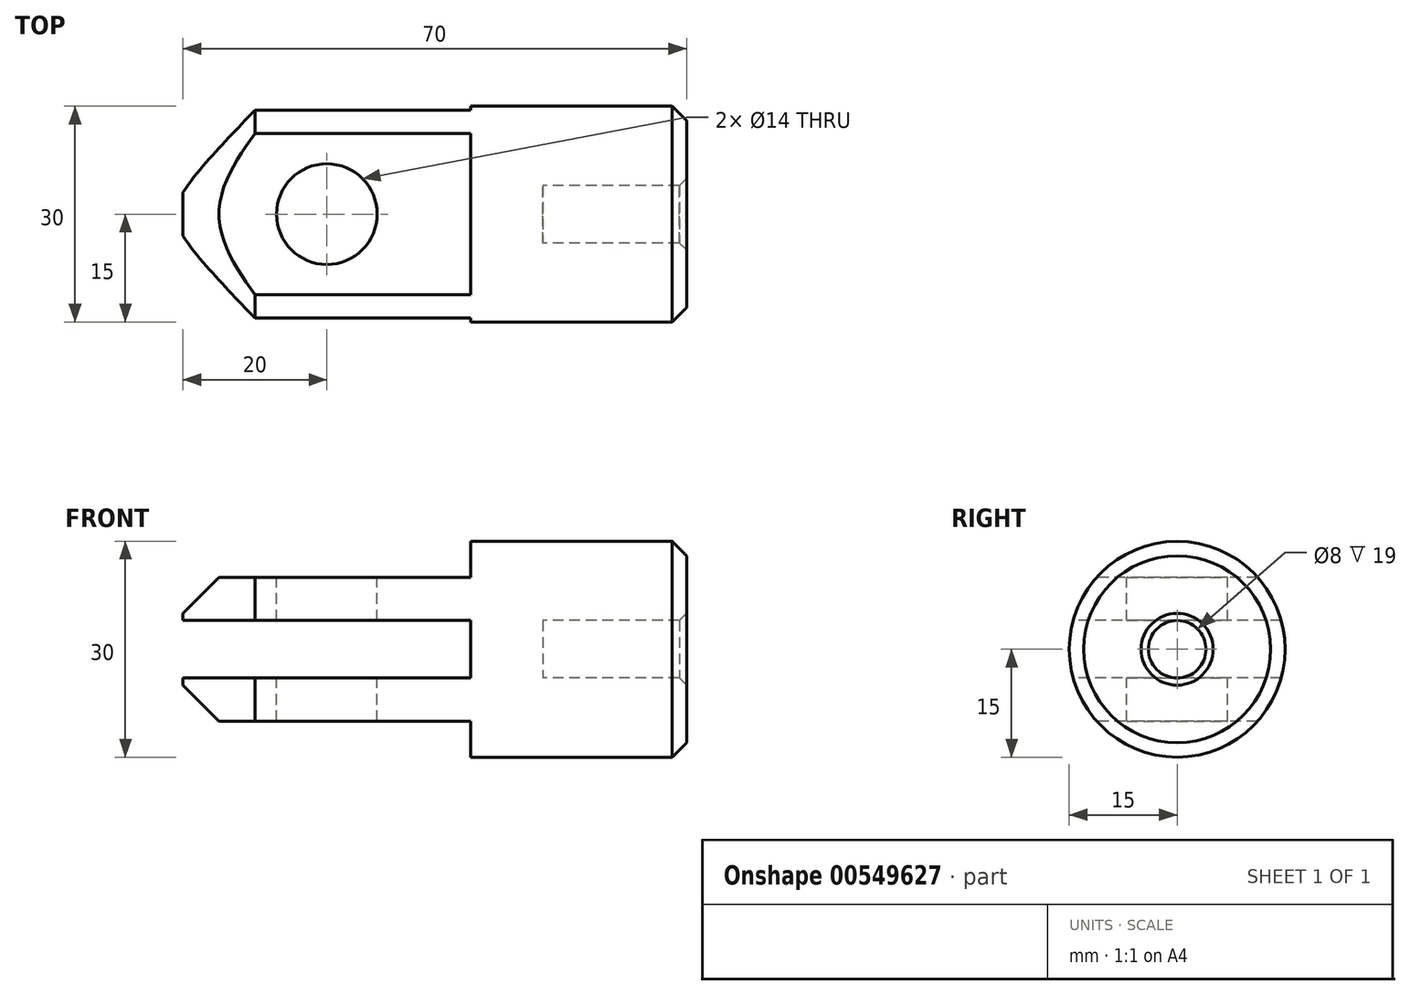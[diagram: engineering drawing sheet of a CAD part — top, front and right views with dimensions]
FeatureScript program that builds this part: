
annotation { "Feature Type Name" : "Feature", "Feature Type Description" : "" }
export const myFeature = defineFeature(function(context is Context, id is Id, definition is map)
    precondition{}
    {
        {
            var Q0;
            Q0=qCreatedBy(makeId("Front.planeOp"),FACE);
            var sketch = newSketch(context, id + "F0", { "sketchPlane" : qUnion([Q0])});
            skLineSegment(sketch, "E0", {"start": v(0, 0) * mm, "end": v(0, 4) * mm});
            skLineSegment(sketch, "E1", {"start": v(0, 4) * mm, "end": v(20, 4) * mm});
            skLineSegment(sketch, "E2", {"start": v(20, 4) * mm, "end": v(20, 15) * mm});
            skLineSegment(sketch, "E3", {"start": v(20, 15) * mm, "end": v(-50, 15) * mm});
            skLineSegment(sketch, "E4", {"start": v(-50, 15) * mm, "end": v(-50, 0) * mm});
            skLineSegment(sketch, "E5", {"start": v(-50, 0) * mm, "end": v(0, 0) * mm});
            skSolve(sketch);
        }
        {
            var Q0;
            Q0=makeQuery(id+"F0.imprint","IMPRINT",FACE,{"disambiguationData":[TD([[makeQuery(id+"F0.imprint","IMPRINT",EDGE,{"derivedFrom":sQuery(id+"F0.wireOp",EDGE,"E0")}),1.0]])]});
            var Q1;
            Q1=sQuery(id+"F0.wireOp",EDGE,"E5");
            revolve(context, id + "F1", {"entities" : qUnion([Q0]), "axis" : qUnion([Q1]), "revolveType" : RevolveType.FULL});
        }
        {
            var Q0;
            Q0=qCreatedBy(makeId("Front.planeOp"),FACE);
            var sketch = newSketch(context, id + "F2", { "sketchPlane" : qUnion([Q0])});
            skLineSegment(sketch, "E6", {"start": v(-60.62, 0) * mm, "end": v(-60.62, 4) * mm});
            skLineSegment(sketch, "E7", {"start": v(-55.02, 4) * mm, "end": v(-10, 4) * mm});
            skLineSegment(sketch, "E8", {"start": v(-60.62, 15) * mm, "end": v(-10, 15) * mm});
            skLineSegment(sketch, "E9.0", {"start": v(-55.02, 10) * mm, "end": v(-10, 10) * mm});
            skPoint(sketch, "E10.endSnap0", {"position": v(0, 15) * mm});
            skLineSegment(sketch, "E11.0", {"start": v(-10, -2) * mm, "end": v(-10, 4) * mm});
            skLineSegment(sketch, "E12", {"start": v(-60.62, 4) * mm, "end": v(-60.62, 15) * mm});
            skPoint(sketch, "E13.orphan", {"position": v(-50, 15) * mm});
            skPoint(sketch, "E14.orphan", {"position": v(0, 19.13) * mm});
            skPoint(sketch, "E15.orphan", {"position": v(50, 15) * mm});
            skLineSegment(sketch, "E16.trimOffspring", {"start": v(-10, 10) * mm, "end": v(-10, 15) * mm});
            skPoint(sketch, "E17.orphan", {"position": v(0, 4) * mm});
            skLineSegment(sketch, "E18", {"start": v(-55.02, 10) * mm, "end": v(-55.02, 4) * mm});
            skPoint(sketch, "E19.orphan", {"position": v(-60.62, 10) * mm});
            skLineSegment(sketch, "E20.MirrorCS", {"start": v(-10, -10) * mm, "end": v(-10, -15) * mm});
            skLineSegment(sketch, "E21.MirrorCS", {"start": v(-55.02, -10) * mm, "end": v(-55.02, -4) * mm});
            skLineSegment(sketch, "E22.MirrorCS", {"start": v(-60.62, -4) * mm, "end": v(-60.62, -15) * mm});
            skLineSegment(sketch, "E23.MirrorCS", {"start": v(-60.62, -15) * mm, "end": v(-10, -15) * mm});
            skLineSegment(sketch, "E24.MirrorCS", {"start": v(-55.02, -4) * mm, "end": v(-10, -4) * mm});
            skLineSegment(sketch, "E25.MirrorCS", {"start": v(-60.62, 0) * mm, "end": v(-60.62, -4) * mm});
            skPoint(sketch, "E26.MirrorP", {"position": v(-60.62, -10) * mm});
            skPoint(sketch, "E27.MirrorP", {"position": v(-50, -15) * mm});
            skLineSegment(sketch, "E28.MirrorCS", {"start": v(-10, 2) * mm, "end": v(-10, -4) * mm});
            skLineSegment(sketch, "E29.MirrorCS", {"start": v(-55.02, -10) * mm, "end": v(-10, -10) * mm});
            skSolve(sketch);
        }
        {
            var Q0;
            Q0=makeQuery(id+"F1.opRevolve","SWEPT_EDGE",EDGE,{"disambiguationData":[OSD([sQuery(id+"F0.wireOp",EDGE,"E3"),sQuery(id+"F0.wireOp",EDGE,"E4")])]});
            chamfer(context, id + "F3", {"entities" : qUnion([Q0]), "width" : 10 * mm, "tangentPropagation" : true});
        }
        {
            var Q0;
            Q0=makeQuery(id+"F2.imprint","IMPRINT",FACE,{"disambiguationData":[TD([[makeQuery(id+"F2.imprint","IMPRINT",EDGE,{"derivedFrom":sQuery(id+"F2.wireOp",EDGE,"E6")}),-1.0]])]});
            extrude(context, id + "F4", {"entities" : qUnion([Q0]), "operationType" : NewBodyOperationType.REMOVE, "endBound" : BoundingType.SYMMETRIC, "oppositeDirection" : true, "depth" : 50 * mm, "offsetDistance" : 25 * mm});
        }
        {
            var Q0;
            Q0=qCreatedBy(makeId("Top.planeOp"),FACE);
            var sketch = newSketch(context, id + "F5", { "sketchPlane" : qUnion([Q0])});
            skCircle(sketch, "E30", {"center": v(-30, 0) * mm, "radius": 7 * mm});
            skSolve(sketch);
        }
        {
            var Q0;
            Q0=makeQuery(id+"F5.imprint","IMPRINT",FACE,{"disambiguationData":[TD([[makeQuery(id+"F5.imprint","IMPRINT",EDGE,{"derivedFrom":sQuery(id+"F5.wireOp",EDGE,"E30")}),1.0]])]});
            var Q1;
            Q1=sQuery(id+"F5.wireOp",EDGE,"E30");
            extrude(context, id + "F6", {"entities" : qUnion([Q0]), "operationType" : NewBodyOperationType.REMOVE, "surfaceEntities" : qUnion([Q1]), "endBound" : BoundingType.SYMMETRIC, "oppositeDirection" : true, "depth" : 50 * mm, "offsetDistance" : 25 * mm});
        }
        {
            var Q0;
            Q0=makeQuery(id+"F1.opRevolve","SWEPT_EDGE",EDGE,{"disambiguationData":[OSD([sQuery(id+"F0.wireOp",EDGE,"E2"),sQuery(id+"F0.wireOp",EDGE,"E3")])]});
            chamfer(context, id + "F7", {"entities" : qUnion([Q0]), "width" : 2 * mm, "tangentPropagation" : true});
        }
        {
            var Q0;
            Q0=makeQuery(id+"F1.opRevolve","SWEPT_EDGE",EDGE,{"disambiguationData":[OSD([sQuery(id+"F0.wireOp",EDGE,"E1"),sQuery(id+"F0.wireOp",EDGE,"E2")])]});
            chamfer(context, id + "F8", {"entities" : qUnion([Q0]), "width" : 1 * mm, "tangentPropagation" : true});
        }
    });
